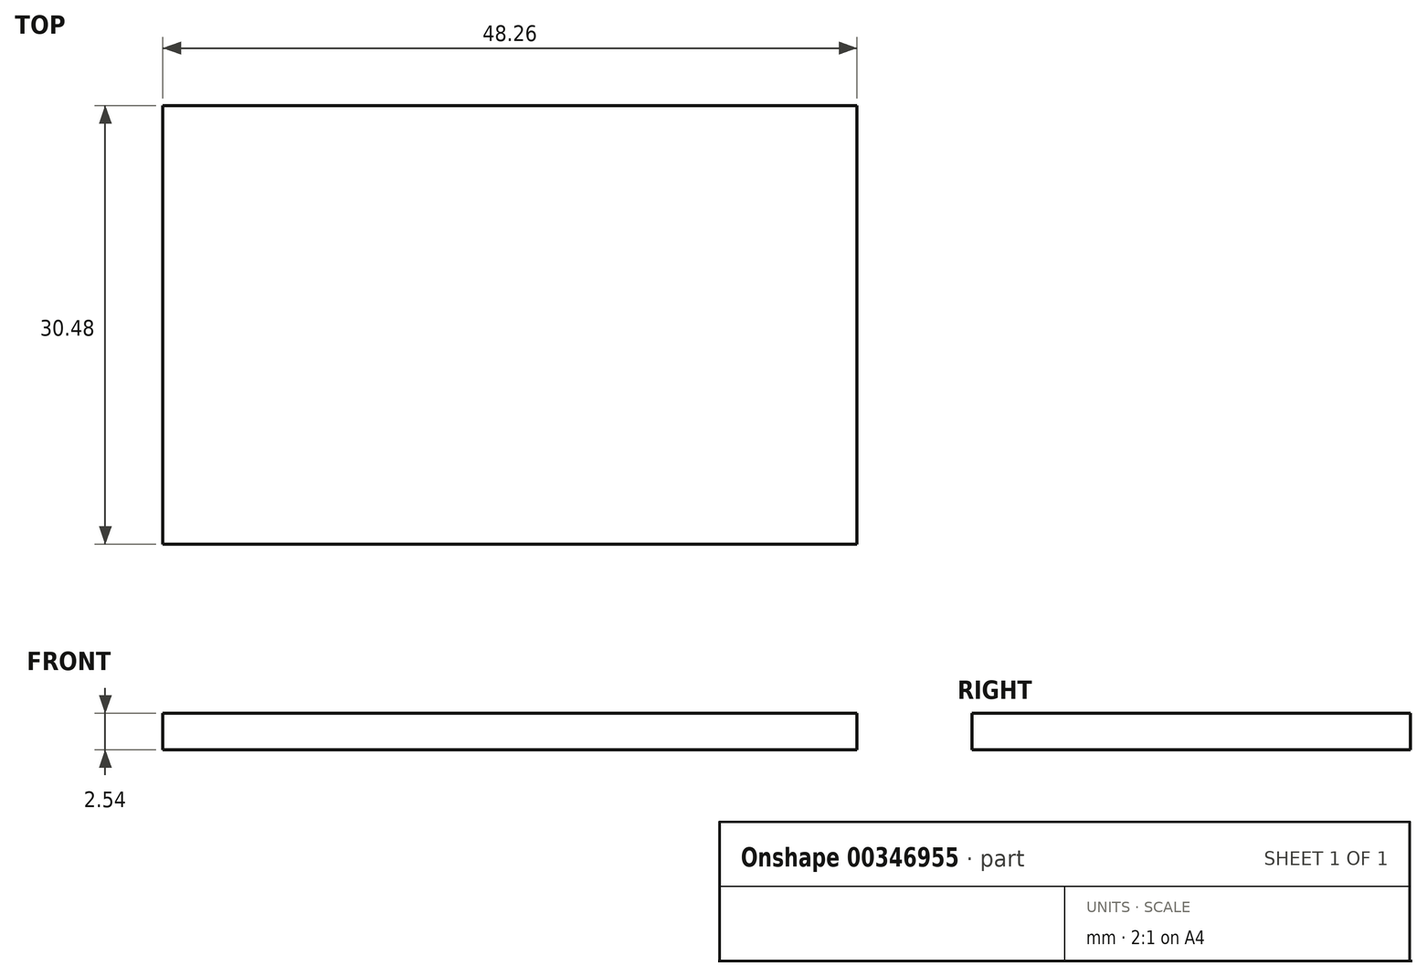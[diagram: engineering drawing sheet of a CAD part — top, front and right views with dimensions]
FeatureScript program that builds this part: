
annotation { "Feature Type Name" : "Feature", "Feature Type Description" : "" }
export const myFeature = defineFeature(function(context is Context, id is Id, definition is map)
    precondition{}
    {
        {
            var Q0;
            Q0=qCreatedBy(makeId("Top.planeOp"),FACE);
            var sketch = newSketch(context, id + "F0", { "sketchPlane" : qUnion([Q0])});
            skLineSegment(sketch, "E0.bottom", {"start": v(24.13, 15.24) * mm, "end": v(-24.13, 15.24) * mm});
            skLineSegment(sketch, "E0.top", {"start": v(24.13, -15.24) * mm, "end": v(-24.13, -15.24) * mm});
            skLineSegment(sketch, "E0.left", {"start": v(24.13, 15.24) * mm, "end": v(24.13, -15.24) * mm});
            skLineSegment(sketch, "E0.right", {"start": v(-24.13, 15.24) * mm, "end": v(-24.13, -15.24) * mm});
            skPoint(sketch, "E0.middle", {"position": v(0, 0) * mm});
            skSolve(sketch);
        }
        {
            var Q0;
            Q0=makeQuery(id+"F0.imprint","IMPRINT",FACE,{"disambiguationData":[TD([[makeQuery(id+"F0.imprint","IMPRINT",EDGE,{"derivedFrom":sQuery(id+"F0.wireOp",EDGE,"E0.bottom")}),1.0]])]});
            extrude(context, id + "F1", {"entities" : qUnion([Q0]), "depth" : 2.54 * mm});
        }
    });
